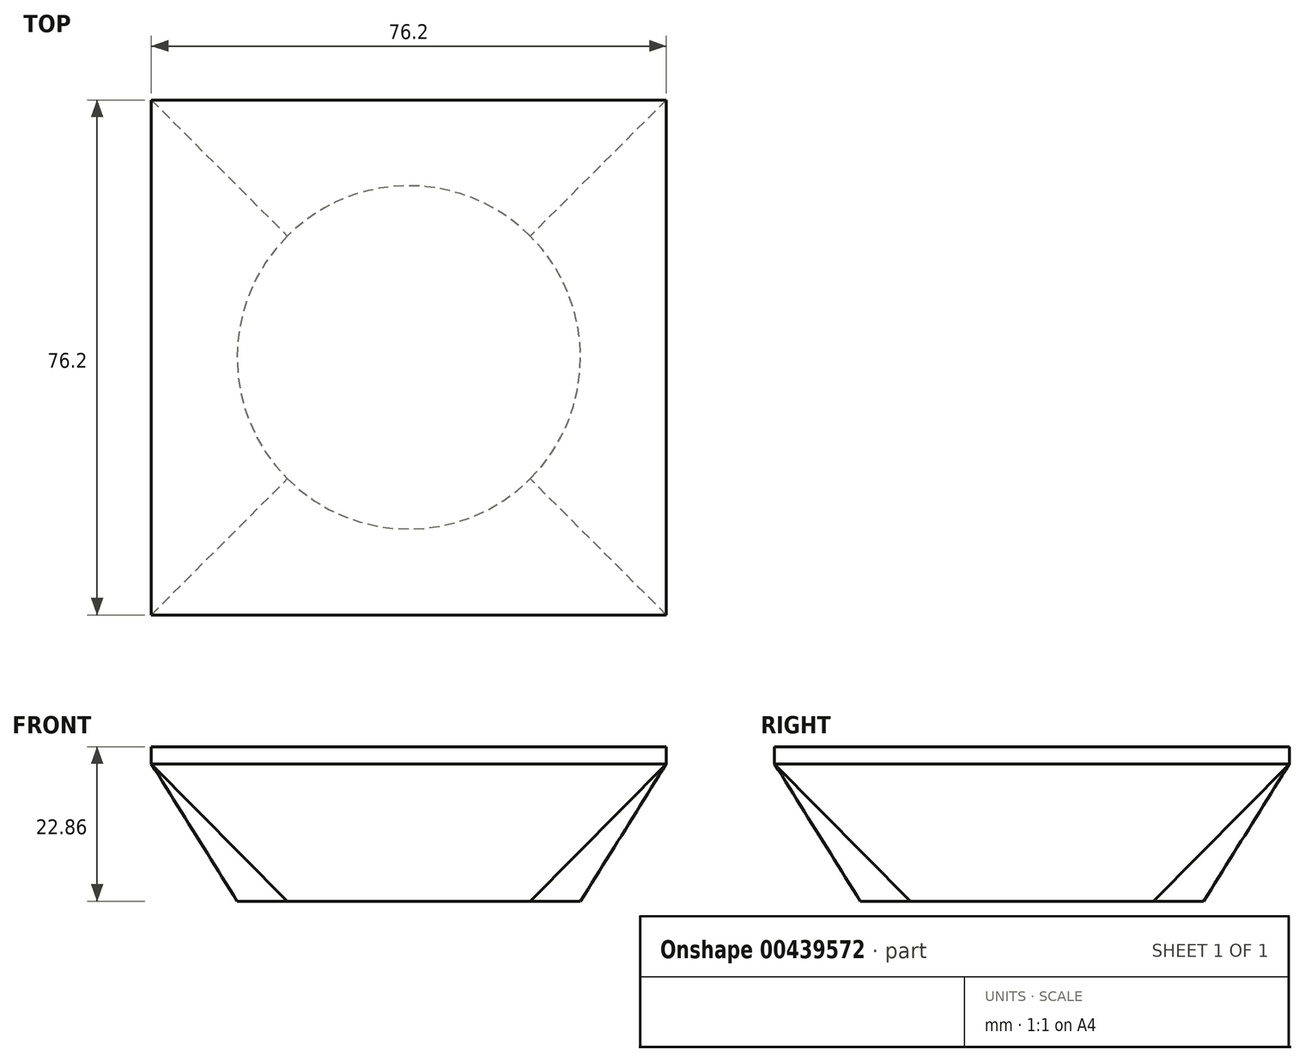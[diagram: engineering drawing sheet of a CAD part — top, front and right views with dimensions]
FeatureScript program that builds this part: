
annotation { "Feature Type Name" : "Feature", "Feature Type Description" : "" }
export const myFeature = defineFeature(function(context is Context, id is Id, definition is map)
    precondition{}
    {
        {
            var Q0;
            Q0=qCreatedBy(makeId("Top.planeOp"),FACE);
            var sketch = newSketch(context, id + "F0", { "sketchPlane" : qUnion([Q0])});
            skCircle(sketch, "E0", {"center": v(0, 0) * mm, "radius": 25.4 * mm});
            skSolve(sketch);
        }
        {
            var Q0;
            Q0=makeQuery(id+"F0.imprint","IMPRINT",FACE,{"disambiguationData":[TD([[makeQuery(id+"F0.imprint","IMPRINT",EDGE,{"derivedFrom":sQuery(id+"F0.wireOp",EDGE,"E0")}),1.0]])]});
            cPlane(context, id + "F1", {"entities" : qUnion([Q0]), "cplaneType" : CPlaneType.OFFSET, "offset" : 25.4 * mm, "width" : 152.4 * mm, "height" : 152.4 * mm});
        }
        {
            var Q0;
            Q0=qCreatedBy(id+"F1.planeOp",FACE);
            var sketch = newSketch(context, id + "F2", { "sketchPlane" : qUnion([Q0])});
            skLineSegment(sketch, "E1", {"start": v(38.1, 0) * mm, "end": v(38.1, 38.1) * mm});
            skLineSegment(sketch, "E2", {"start": v(38.1, 0) * mm, "end": v(38.1, -38.1) * mm});
            skLineSegment(sketch, "E3", {"start": v(38.1, 38.1) * mm, "end": v(-38.1, 38.1) * mm});
            skLineSegment(sketch, "E4", {"start": v(-38.1, 38.1) * mm, "end": v(-38.1, -38.1) * mm});
            skLineSegment(sketch, "E5", {"start": v(-38.1, -38.1) * mm, "end": v(38.1, -38.1) * mm});
            skPoint(sketch, "E6.end.orphan", {"position": v(-38.1, 0) * mm});
            skSolve(sketch);
        }
        {
            var Q0;
            Q0=makeQuery(id+"F0.imprint","IMPRINT",FACE,{"disambiguationData":[TD([[makeQuery(id+"F0.imprint","IMPRINT",EDGE,{"derivedFrom":sQuery(id+"F0.wireOp",EDGE,"E0")}),1.0]])]});
            extrude(context, id + "F3", {"entities" : qUnion([Q0]), "depth" : 2.54 * mm});
        }
        {
            var Q0;
            Q0=makeQuery(id+"F2.imprint","IMPRINT",FACE,{"disambiguationData":[TD([[makeQuery(id+"F2.imprint","IMPRINT",EDGE,{"derivedFrom":sQuery(id+"F2.wireOp",EDGE,"E1")}),1.0]])]});
            extrude(context, id + "F4", {"entities" : qUnion([Q0]), "operationType" : NewBodyOperationType.ADD, "oppositeDirection" : true, "depth" : 2.54 * mm});
        }
        {
            var Q1;
            Q1=makeQuery(id+"F4.opExtrude","CAP_FACE",FACE,{"disambiguationData":[OSD([sQuery(id+"F2.wireOp",EDGE,"E1"),sQuery(id+"F2.wireOp",EDGE,"E2"),sQuery(id+"F2.wireOp",EDGE,"E3"),sQuery(id+"F2.wireOp",EDGE,"E4"),sQuery(id+"F2.wireOp",EDGE,"E5")])],"isStart":false});
            var Q2;
            Q2=makeQuery(id+"F3.opExtrude","CAP_FACE",FACE,{"disambiguationData":[OSD([sQuery(id+"F0.wireOp",EDGE,"E0")])],"isStart":false});
            loft(context, id + "F5", {"operationType" : NewBodyOperationType.ADD, "sheetProfilesArray" : [{ "sheetProfileEntities" : qUnion([Q1]) }, { "sheetProfileEntities" : qUnion([Q2]) }]});
        }
        {
            var Q0;
            Q0=makeQuery(id+"F3.opExtrude","CAP_FACE",FACE,{"disambiguationData":[OSD([sQuery(id+"F0.wireOp",EDGE,"E0")])],"isStart":true});
            extrude(context, id + "F6", {"entities" : qUnion([Q0]), "operationType" : NewBodyOperationType.REMOVE, "oppositeDirection" : true, "depth" : 2.54 * mm});
        }
    });
